# Revit family: Furniture_Chairs-Stools-Benches_Gotessons_Office-Nap_
name_source: partatom
category: Furniture
revit_build: Autodesk Revit 2015 (Build: 20140903_1530(x64)
units: mm (PartAtom-declared; Revit-internal decimal feet)

## types (1)
- Default
    BIMobject category = Chairs, Stools & Benches
    BIMobject category code = furniture-chairs-stools-benches
    BIMobject main category = Furniture
    BIMobject main category code = furniture
    BOSUseNativeGeometries = 1
    Brand url = http://www.gotessons.se
    Design country = Sweden
    Edition number = 1
    IFC Classification = Furnishing Element
    Manufacturer country = Sweden
    Manufacturer name = Götessons
    Masterformat 2014 Code = 12 50 00
    Masterformat 2014 Description = Furniture
    Material main = Fabric
    Material secondary = Fabric
    Product Guid = e2695ea0-7ca3-4230-ad7b-840b420f1d30
    Product SKU = office_nap
    Product certification = https://www.gotessons.com
    Product data url = https://bimobject.com
    Product family = Furniture
    Product group = Chairs, Stools & Benches
    Product name = Office Nap
    Product url = https://www.gotessons.com
    QR code = http://bimobject.com
    Technical description = https://www.gotessons.com
    UNSPSC Code = 56
    Uniclass 1.4 Code = L8211
    Uniclass 1.4 Description = Furniture
    Uniclass 2015 Code = Pr_40_50
    Uniclass 2015 Name = Furnishings
    Uniformat II Code = E20
    Uniformat II Description = FURNISHINGS

## geometry (parser evidence)
native form markers: Sweep x3
no freeform markers — native parametric forms only
